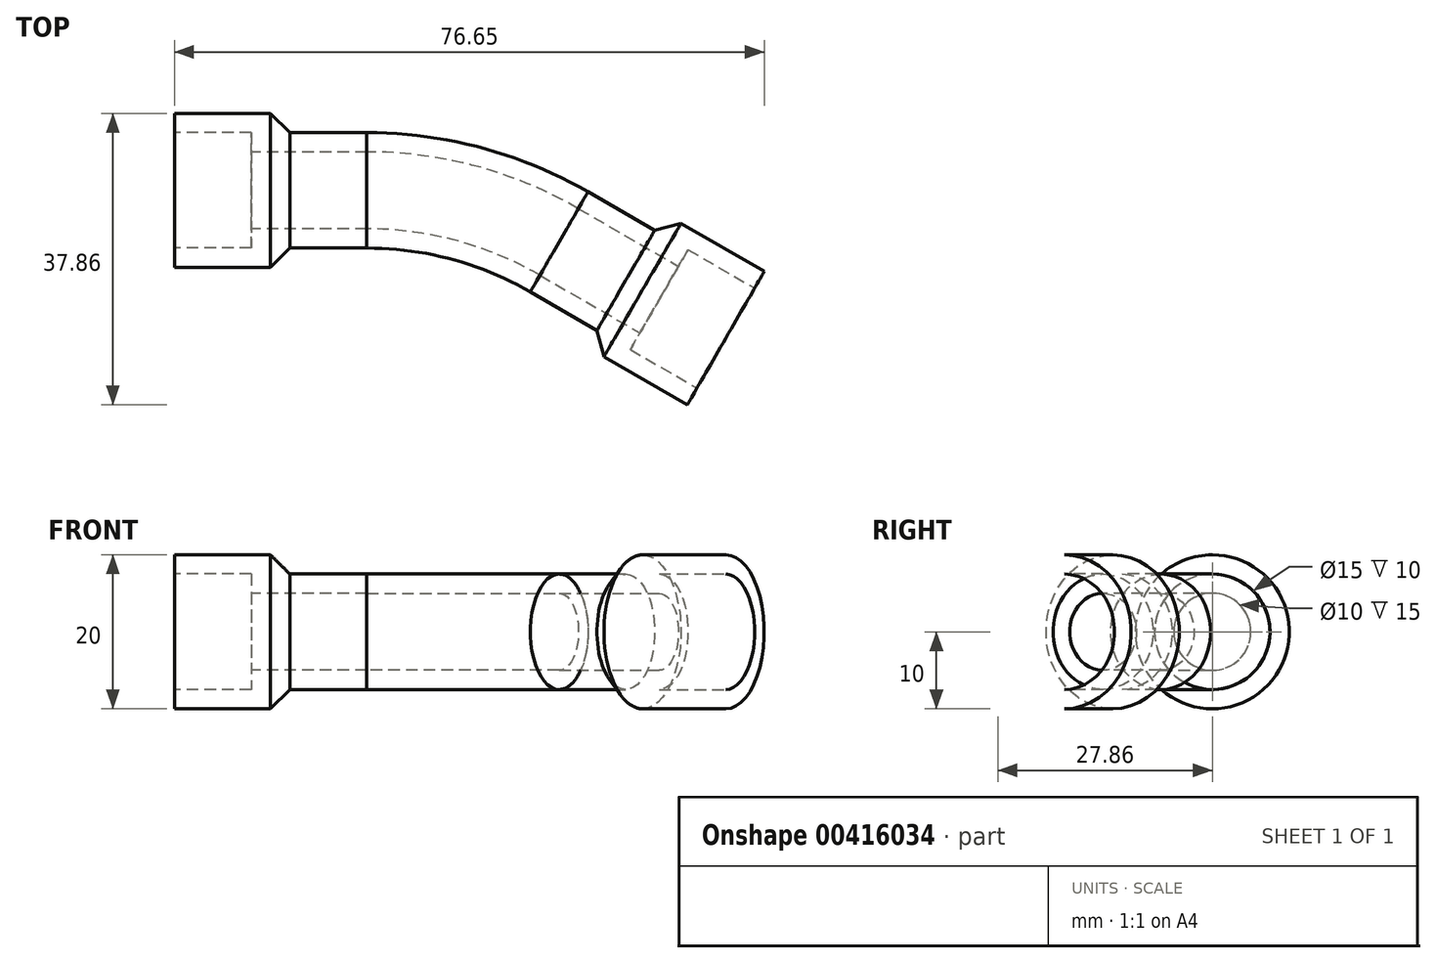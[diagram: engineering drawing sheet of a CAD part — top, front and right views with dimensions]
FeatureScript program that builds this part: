
annotation { "Feature Type Name" : "Feature", "Feature Type Description" : "" }
export const myFeature = defineFeature(function(context is Context, id is Id, definition is map)
    precondition{}
    {
        {
            assignVariable(context, id + "F0", {"name" : "Angle", "anyValue" : 30});
        }
        {
            var Q0;
            Q0=qCreatedBy(makeId("Top.planeOp"),FACE);
            var sketch = newSketch(context, id + "F1", { "sketchPlane" : qUnion([Q0])});
            skLineSegment(sketch, "E0", {"start": v(0, 0) * mm, "end": v(50, 0) * mm, "construction": true});
            skLineSegment(sketch, "E1", {"start": v(-15, 7.5) * mm, "end": v(-25, 7.5) * mm});
            skLineSegment(sketch, "E2", {"start": v(-25, 7.5) * mm, "end": v(-25, 10) * mm});
            skLineSegment(sketch, "E3", {"start": v(-25, 10) * mm, "end": v(-12.5, 10) * mm});
            skLineSegment(sketch, "E4", {"start": v(-12.5, 10) * mm, "end": v(-10, 7.5) * mm});
            skLineSegment(sketch, "E5", {"start": v(-10, 7.5) * mm, "end": v(0, 7.5) * mm});
            skLineSegment(sketch, "E6", {"start": v(0, 7.5) * mm, "end": v(0, 5) * mm});
            skLineSegment(sketch, "E7", {"start": v(0, 5) * mm, "end": v(-15, 5) * mm});
            skLineSegment(sketch, "E8", {"start": v(-15, 5) * mm, "end": v(-15, 7.5) * mm});
            skLineSegment(sketch, "E9", {"start": v(-15, 7.5) * mm, "end": v(-12.5, 10) * mm, "construction": true});
            skArc(sketch, "E10", {"start": v(25, -6.7) * mm, "mid": v(12.94, -1.7) * mm, "end": v(0, 0) * mm});
            skLineSegment(sketch, "E11", {"start": v(25, -6.7) * mm, "end": v(0, -50) * mm, "construction": true});
            skLineSegment(sketch, "E12", {"start": v(0, 0) * mm, "end": v(0, -50) * mm, "construction": true});
            skSolve(sketch);
        }
        {
            var Q0;
            Q0=qCreatedBy(makeId("Right.planeOp"),FACE);
            var sketch = newSketch(context, id + "F2", { "sketchPlane" : qUnion([Q0])});
            skLineSegment(sketch, "E13", {"start": v(-50, 50.44) * mm, "end": v(-50, -52.93) * mm, "construction": true});
            skSolve(sketch);
        }
        {
            var Q0;
            Q0=makeQuery(id+"F1.imprint","IMPRINT",FACE,{"disambiguationData":[TD([[makeQuery(id+"F1.imprint","IMPRINT",EDGE,{"derivedFrom":sQuery(id+"F1.wireOp",EDGE,"E1")}),-1.0]])]});
            var Q1;
            Q1=sQuery(id+"F1.wireOp",EDGE,"E0");
            revolve(context, id + "F3", {"entities" : qUnion([Q0]), "axis" : qUnion([Q1]), "revolveType" : RevolveType.FULL});
        }
        {
            var Q0;
            Q0=makeQuery(id+"F3.opRevolve","SWEPT_FACE",FACE,{"disambiguationData":[OSD([sQuery(id+"F1.wireOp",EDGE,"E6")])]});
            var Q1;
            Q1=sQuery(id+"F1.wireOp",EDGE,"E10");
            sweep(context, id + "F4", {"profiles" : qUnion([Q0]), "path" : qUnion([Q1])});
        }
        {
            var Q0;
            Q0=makeQuery(id+"F3.opRevolve","SWEPT_BODY",BODY,{"disambiguationData":[OSD([sQuery(id+"F1.wireOp",EDGE,"E1"),sQuery(id+"F1.wireOp",EDGE,"E2"),sQuery(id+"F1.wireOp",EDGE,"E3"),sQuery(id+"F1.wireOp",EDGE,"E4"),sQuery(id+"F1.wireOp",EDGE,"E5"),sQuery(id+"F1.wireOp",EDGE,"E6"),sQuery(id+"F1.wireOp",EDGE,"E7"),sQuery(id+"F1.wireOp",EDGE,"E8")])]});
            var Q1;
            Q1=qCreatedBy(makeId("Right.planeOp"),FACE);
            mirror(context, id + "F5", {"entities" : qUnion([Q0]), "mirrorPlane" : qUnion([Q1])});
        }
        {
            var Q0;
            Q0=makeQuery(id+"F5.opPattern","COPY",BODY,{"derivedFrom":makeQuery(id+"F3.opRevolve","SWEPT_BODY",BODY,{"disambiguationData":[OSD([sQuery(id+"F1.wireOp",EDGE,"E1"),sQuery(id+"F1.wireOp",EDGE,"E2"),sQuery(id+"F1.wireOp",EDGE,"E3"),sQuery(id+"F1.wireOp",EDGE,"E4"),sQuery(id+"F1.wireOp",EDGE,"E5"),sQuery(id+"F1.wireOp",EDGE,"E6"),sQuery(id+"F1.wireOp",EDGE,"E7"),sQuery(id+"F1.wireOp",EDGE,"E8")])]}),"instanceName":"1"});
            var Q1;
            Q1=sQuery(id+"F2.wireOp",EDGE,"E13");
            transform(context, id + "F6", {"entities" : qUnion([Q0]), "transformType" : TransformType.ROTATION, "transformAxis" : qUnion([Q1]), "angle" : (getVariable(context, 'Angle')) * degree, "makeCopy" : false});
        }
    });
